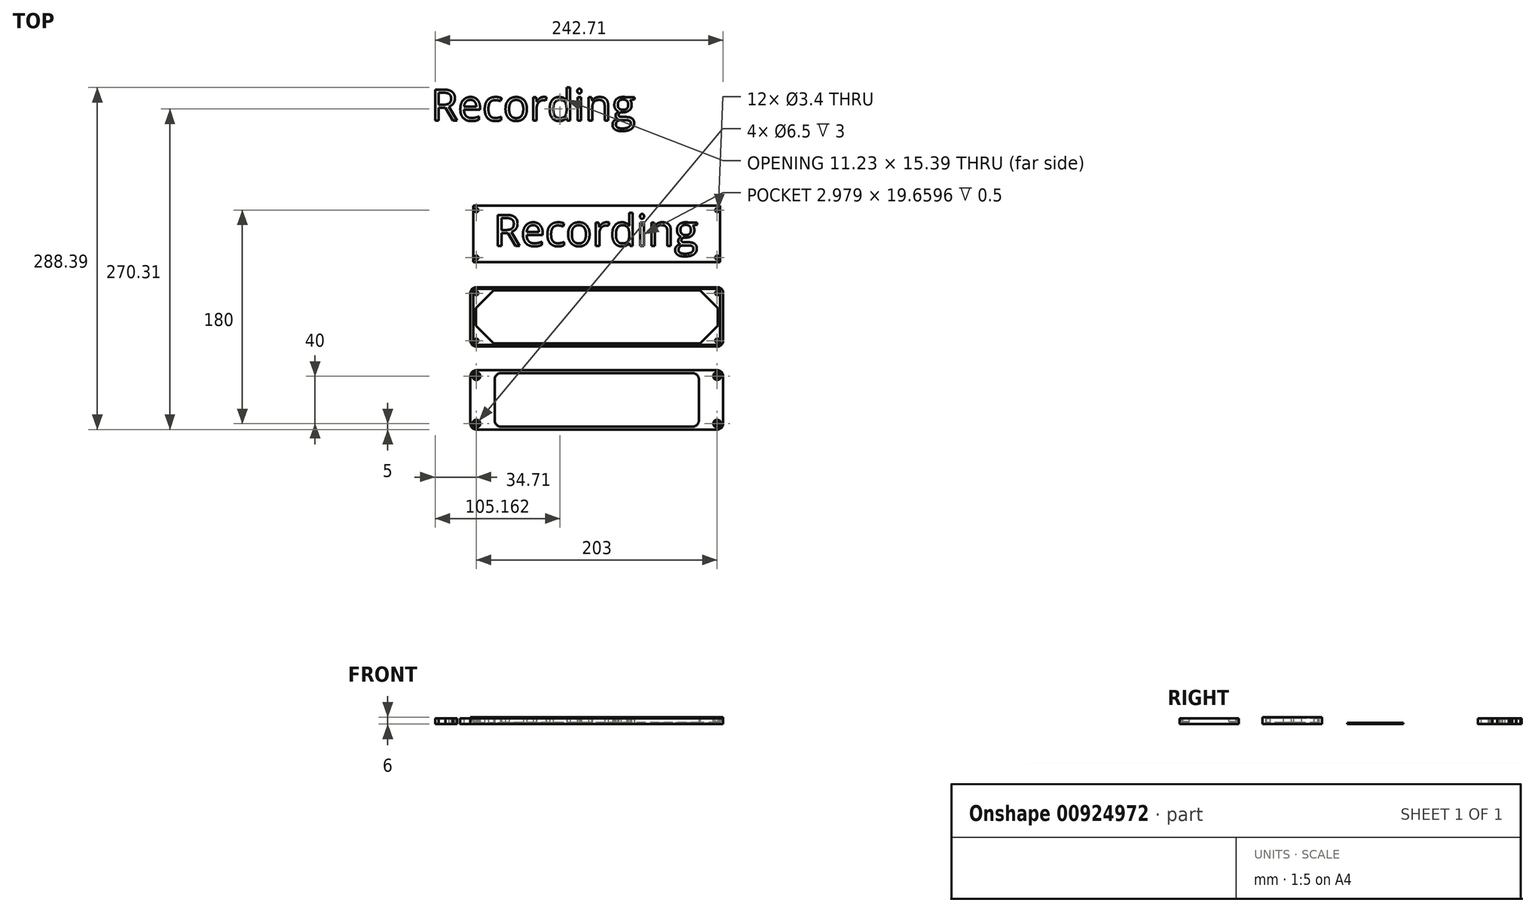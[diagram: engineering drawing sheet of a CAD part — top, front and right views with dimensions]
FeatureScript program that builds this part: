
annotation { "Feature Type Name" : "Feature", "Feature Type Description" : "" }
export const myFeature = defineFeature(function(context is Context, id is Id, definition is map)
    precondition{}
    {
        {
            var Q0;
            Q0=qCreatedBy(makeId("Top.planeOp"),FACE);
            var sketch = newSketch(context, id + "F0", { "sketchPlane" : qUnion([Q0])});
            skLineSegment(sketch, "E0.bottom", {"start": v(0, 0) * mm, "end": v(87, 0) * mm});
            skLineSegment(sketch, "E0.top", {"start": v(0, -45) * mm, "end": v(87, -45) * mm});
            skLineSegment(sketch, "E1.bottom", {"start": v(0, 0) * mm, "end": v(-87, 0) * mm});
            skLineSegment(sketch, "E1.top", {"start": v(0, -45) * mm, "end": v(-87, -45) * mm});
            skLineSegment(sketch, "E2", {"start": v(87, 0) * mm, "end": v(102, -15) * mm});
            skLineSegment(sketch, "E3", {"start": v(102, -15) * mm, "end": v(102, -30) * mm});
            skLineSegment(sketch, "E4", {"start": v(102, -30) * mm, "end": v(87, -45) * mm});
            skLineSegment(sketch, "E5", {"start": v(-87, 0) * mm, "end": v(-102, -15) * mm});
            skLineSegment(sketch, "E6", {"start": v(-102, -15) * mm, "end": v(-102, -30) * mm});
            skLineSegment(sketch, "E7", {"start": v(-102, -30) * mm, "end": v(-87, -45) * mm});
            skLineSegment(sketch, "E8.bottom", {"start": v(102, -21.5) * mm, "end": v(104, -21.5) * mm});
            skLineSegment(sketch, "E8.top", {"start": v(102, -23.5) * mm, "end": v(104, -23.5) * mm});
            skLineSegment(sketch, "E8.left", {"start": v(102, -21.5) * mm, "end": v(102, -23.5) * mm});
            skLineSegment(sketch, "E8.right", {"start": v(104, -21.5) * mm, "end": v(104, -23.5) * mm});
            skLineSegment(sketch, "E9.bottom", {"start": v(-102, -21.5) * mm, "end": v(-104, -21.5) * mm});
            skLineSegment(sketch, "E9.top", {"start": v(-102, -23.5) * mm, "end": v(-104, -23.5) * mm});
            skLineSegment(sketch, "E9.left", {"start": v(-102, -21.5) * mm, "end": v(-102, -23.5) * mm});
            skLineSegment(sketch, "E9.right", {"start": v(-104, -21.5) * mm, "end": v(-104, -23.5) * mm});
            skLineSegment(sketch, "E10.bottom", {"start": v(106.5, 2.5) * mm, "end": v(-106.5, 2.5) * mm});
            skLineSegment(sketch, "E10.top", {"start": v(106.5, -47.5) * mm, "end": v(-106.5, -47.5) * mm});
            skLineSegment(sketch, "E10.left", {"start": v(106.5, 2.5) * mm, "end": v(106.5, -47.5) * mm});
            skLineSegment(sketch, "E10.right", {"start": v(-106.5, 2.5) * mm, "end": v(-106.5, -47.5) * mm});
            skSolve(sketch);
        }
        {
            var Q0;
            Q0 = qSketchRegion(id + "F0", true);
            extrude(context, id + "F1", {"entities" : qUnion([Q0]), "depth" : 5 * mm, "offsetDistance" : 25 * mm});
        }
        {
            var Q0;
            Q0=makeQuery(id+"F0.imprint","IMPRINT",FACE,{"disambiguationData":[TD([[makeQuery(id+"F0.imprint","IMPRINT",EDGE,{"derivedFrom":sQuery(id+"F0.wireOp",EDGE,"E0.bottom")}),-1.0]])]});
            extrude(context, id + "F2", {"entities" : qUnion([Q0]), "operationType" : NewBodyOperationType.ADD, "depth" : 1.4 * mm, "offsetDistance" : 25 * mm});
        }
        {
            var Q0;
            Q0=makeQuery(id+"F1.opExtrude","CAP_FACE",FACE,{"disambiguationData":[OSD([sQuery(id+"F0.wireOp",EDGE,"E0.bottom"),sQuery(id+"F0.wireOp",EDGE,"E0.top"),sQuery(id+"F0.wireOp",EDGE,"E1.bottom"),sQuery(id+"F0.wireOp",EDGE,"E1.top"),sQuery(id+"F0.wireOp",EDGE,"E2"),sQuery(id+"F0.wireOp",EDGE,"E3"),sQuery(id+"F0.wireOp",EDGE,"E4"),sQuery(id+"F0.wireOp",EDGE,"E5"),sQuery(id+"F0.wireOp",EDGE,"E6"),sQuery(id+"F0.wireOp",EDGE,"E7"),sQuery(id+"F0.wireOp",EDGE,"E8.bottom"),sQuery(id+"F0.wireOp",EDGE,"E8.top"),sQuery(id+"F0.wireOp",EDGE,"E8.right"),sQuery(id+"F0.wireOp",EDGE,"E9.bottom"),sQuery(id+"F0.wireOp",EDGE,"E9.top"),sQuery(id+"F0.wireOp",EDGE,"E9.right"),sQuery(id+"F0.wireOp",EDGE,"E10.bottom"),sQuery(id+"F0.wireOp",EDGE,"E10.top"),sQuery(id+"F0.wireOp",EDGE,"E10.left"),sQuery(id+"F0.wireOp",EDGE,"E10.right")])],"isStart":false});
            var sketch = newSketch(context, id + "F3", { "sketchPlane" : qUnion([Q0])});
            skLineSegment(sketch, "E11.bottom", {"start": v(-106.5, 2.5) * mm, "end": v(106.5, 2.5) * mm});
            skLineSegment(sketch, "E11.top", {"start": v(-106.5, -47.5) * mm, "end": v(106.5, -47.5) * mm});
            skLineSegment(sketch, "E11.left", {"start": v(-106.5, 2.5) * mm, "end": v(-106.5, -47.5) * mm});
            skLineSegment(sketch, "E11.right", {"start": v(106.5, 2.5) * mm, "end": v(106.5, -47.5) * mm});
            skLineSegment(sketch, "E12.bottom", {"start": v(-104, 1.25) * mm, "end": v(104, 1.25) * mm});
            skLineSegment(sketch, "E12.top", {"start": v(-104, -46.25) * mm, "end": v(104, -46.25) * mm});
            skLineSegment(sketch, "E12.left", {"start": v(-104, 1.25) * mm, "end": v(-104, -46.25) * mm});
            skLineSegment(sketch, "E12.right", {"start": v(104, 1.25) * mm, "end": v(104, -46.25) * mm});
            skSolve(sketch);
        }
        {
            var Q0;
            Q0=makeQuery(id+"F3.imprint","IMPRINT",FACE,{"disambiguationData":[TD([[makeQuery(id+"F3.imprint","IMPRINT",EDGE,{"derivedFrom":sQuery(id+"F3.wireOp",EDGE,"E11.bottom")}),1.0]])]});
            extrude(context, id + "F4", {"entities" : qUnion([Q0]), "operationType" : NewBodyOperationType.ADD, "depth" : 1 * mm, "offsetDistance" : 25 * mm});
        }
        {
            var Q0;
            Q0=makeQuery(id+"F4.opExtrude","CAP_FACE",FACE,{"disambiguationData":[OSD([sQuery(id+"F3.wireOp",EDGE,"E11.bottom"),sQuery(id+"F3.wireOp",EDGE,"E11.top"),sQuery(id+"F3.wireOp",EDGE,"E11.left"),sQuery(id+"F3.wireOp",EDGE,"E11.right"),sQuery(id+"F3.wireOp",EDGE,"p96hWnhM-O248-CkP6-rmGI-8VL5oQeekFGz.bottom"),sQuery(id+"F3.wireOp",EDGE,"p96hWnhM-O248-CkP6-rmGI-8VL5oQeekFGz.top"),sQuery(id+"F3.wireOp",EDGE,"tadGcO1i-splK-dY1s-Agr0-QRfTQJM7h8ux"),sQuery(id+"F3.wireOp",EDGE,"MCb5JSWs-usyO-wEvL-fpDv-uoKTlJ5k66d6"),sQuery(id+"F3.wireOp",EDGE,"NITJUnnU-xe1N-w4uj-sHKg-5JDy11YuTqra"),sQuery(id+"F3.wireOp",EDGE,"5tmfxtAg-Ul8O-jr4B-bajV-lyweOX73wN6o"),sQuery(id+"F3.wireOp",EDGE,"gdZn3bBH-IIBM-45FK-eHiO-CvuzcM1Qr1wt"),sQuery(id+"F3.wireOp",EDGE,"ff11BVGO-ZWvE-YObo-sifm-qKeFPP4lbaiZ")])],"isStart":false});
            var sketch = newSketch(context, id + "F5", { "sketchPlane" : qUnion([Q0])});
            skLineSegment(sketch, "E13.bottom", {"start": v(-106.5, 2.5) * mm, "end": v(-96.5, 2.5) * mm, "construction": true});
            skLineSegment(sketch, "E13.top", {"start": v(-106.5, -7.5) * mm, "end": v(-96.5, -7.5) * mm, "construction": true});
            skLineSegment(sketch, "E13.left", {"start": v(-106.5, 2.5) * mm, "end": v(-106.5, -7.5) * mm, "construction": true});
            skLineSegment(sketch, "E13.right", {"start": v(-96.5, 2.5) * mm, "end": v(-96.5, -7.5) * mm, "construction": true});
            skLineSegment(sketch, "E14.bottom", {"start": v(-106.5, -47.5) * mm, "end": v(-96.5, -47.5) * mm, "construction": true});
            skLineSegment(sketch, "E14.top", {"start": v(-106.5, -37.5) * mm, "end": v(-96.5, -37.5) * mm, "construction": true});
            skLineSegment(sketch, "E14.left", {"start": v(-106.5, -47.5) * mm, "end": v(-106.5, -37.5) * mm, "construction": true});
            skLineSegment(sketch, "E14.right", {"start": v(-96.5, -47.5) * mm, "end": v(-96.5, -37.5) * mm, "construction": true});
            skLineSegment(sketch, "E15.bottom", {"start": v(106.5, -47.5) * mm, "end": v(96.5, -47.5) * mm, "construction": true});
            skLineSegment(sketch, "E15.top", {"start": v(106.5, -37.5) * mm, "end": v(96.5, -37.5) * mm, "construction": true});
            skLineSegment(sketch, "E15.left", {"start": v(106.5, -47.5) * mm, "end": v(106.5, -37.5) * mm, "construction": true});
            skLineSegment(sketch, "E15.right", {"start": v(96.5, -47.5) * mm, "end": v(96.5, -37.5) * mm, "construction": true});
            skLineSegment(sketch, "E16.bottom", {"start": v(106.5, 2.5) * mm, "end": v(96.5, 2.5) * mm, "construction": true});
            skLineSegment(sketch, "E16.top", {"start": v(106.5, -7.5) * mm, "end": v(96.5, -7.5) * mm, "construction": true});
            skLineSegment(sketch, "E16.left", {"start": v(106.5, 2.5) * mm, "end": v(106.5, -7.5) * mm, "construction": true});
            skLineSegment(sketch, "E16.right", {"start": v(96.5, 2.5) * mm, "end": v(96.5, -7.5) * mm, "construction": true});
            skLineSegment(sketch, "E17", {"start": v(-106.5, 2.5) * mm, "end": v(-96.5, -7.5) * mm, "construction": true});
            skLineSegment(sketch, "E18", {"start": v(-106.5, -7.5) * mm, "end": v(-96.5, 2.5) * mm, "construction": true});
            skLineSegment(sketch, "E19", {"start": v(-106.5, -37.5) * mm, "end": v(-96.5, -47.5) * mm, "construction": true});
            skLineSegment(sketch, "E20", {"start": v(-106.5, -47.5) * mm, "end": v(-96.5, -37.5) * mm, "construction": true});
            skLineSegment(sketch, "E21", {"start": v(96.5, -47.5) * mm, "end": v(106.5, -37.5) * mm, "construction": true});
            skLineSegment(sketch, "E22", {"start": v(96.5, -37.5) * mm, "end": v(106.5, -47.5) * mm, "construction": true});
            skLineSegment(sketch, "E23", {"start": v(96.5, 2.5) * mm, "end": v(106.5, -7.5) * mm, "construction": true});
            skLineSegment(sketch, "E24", {"start": v(96.5, -7.5) * mm, "end": v(106.5, 2.5) * mm, "construction": true});
            skPoint(sketch, "E25", {"position": v(-101.5, -2.5) * mm});
            skPoint(sketch, "E26", {"position": v(-101.5, -42.5) * mm});
            skPoint(sketch, "E27", {"position": v(101.5, -2.5) * mm});
            skPoint(sketch, "E28", {"position": v(101.5, -42.5) * mm});
            skSolve(sketch);
        }
        {
            var Q0;
            Q0=sQuery(id+"F5.wireOp",VERTEX,"E25");
            var Q1;
            Q1=sQuery(id+"F5.wireOp",VERTEX,"E26");
            var Q2;
            Q2=sQuery(id+"F5.wireOp",VERTEX,"E28");
            var Q3;
            Q3=sQuery(id+"F5.wireOp",VERTEX,"E27");
            var Q4;
            Q4=makeQuery(id+"F1.opExtrude","SWEPT_BODY",BODY,{"disambiguationData":[OSD([sQuery(id+"F0.wireOp",EDGE,"E0.bottom"),sQuery(id+"F0.wireOp",EDGE,"E0.top"),sQuery(id+"F0.wireOp",EDGE,"E1.bottom"),sQuery(id+"F0.wireOp",EDGE,"E1.top"),sQuery(id+"F0.wireOp",EDGE,"E2"),sQuery(id+"F0.wireOp",EDGE,"E3"),sQuery(id+"F0.wireOp",EDGE,"E4"),sQuery(id+"F0.wireOp",EDGE,"E5"),sQuery(id+"F0.wireOp",EDGE,"E6"),sQuery(id+"F0.wireOp",EDGE,"E7"),sQuery(id+"F0.wireOp",EDGE,"E8.bottom"),sQuery(id+"F0.wireOp",EDGE,"E8.top"),sQuery(id+"F0.wireOp",EDGE,"E8.right"),sQuery(id+"F0.wireOp",EDGE,"E9.bottom"),sQuery(id+"F0.wireOp",EDGE,"E9.top"),sQuery(id+"F0.wireOp",EDGE,"E9.right"),sQuery(id+"F0.wireOp",EDGE,"E10.bottom"),sQuery(id+"F0.wireOp",EDGE,"E10.top"),sQuery(id+"F0.wireOp",EDGE,"E10.left"),sQuery(id+"F0.wireOp",EDGE,"E10.right")])]});
            hole(context, id + "F6", {"style" : HoleStyle.SIMPLE, "endStyle" : HoleEndStyle.BLIND, "standardTappedOrClearance" : lookupTablePath({ "fit" : "Normal", "standard" : "ISO", "size" : "M3", "type" : "Clearance" }), "standardBlindInLast" : lookupTablePath({ "fit" : "Normal", "standard" : "ISO", "engagement" : "75%", "pitch" : "0.5 mm", "size" : "M3", "type" : "Clearance & tapped" }), "holeDiameter" : 3.4 * mm, "majorDiameter" : 5 * mm, "holeDepth" : 7 * mm, "isTappedThrough" : true, "tappedDepth" : 12 * mm, "tapClearance" : 3, "startFromSketch" : true, "locations" : qUnion([Q0, Q1, Q2, Q3]), "scope" : qUnion([Q4])});
        }
        {
            var Q0;
            Q0=makeQuery(id+"F1.opExtrude","SWEPT_EDGE",EDGE,{"disambiguationData":[OSD([sQuery(id+"F0.wireOp",EDGE,"E10.bottom"),sQuery(id+"F0.wireOp",EDGE,"E10.right")])]});
            var Q1;
            Q1=makeQuery(id+"F1.opExtrude","SWEPT_EDGE",EDGE,{"disambiguationData":[OSD([sQuery(id+"F0.wireOp",EDGE,"E10.top"),sQuery(id+"F0.wireOp",EDGE,"E10.right")])]});
            var Q2;
            Q2=makeQuery(id+"F1.opExtrude","SWEPT_EDGE",EDGE,{"disambiguationData":[OSD([sQuery(id+"F0.wireOp",EDGE,"E10.top"),sQuery(id+"F0.wireOp",EDGE,"E10.left")])]});
            var Q3;
            Q3=makeQuery(id+"F1.opExtrude","SWEPT_EDGE",EDGE,{"disambiguationData":[OSD([sQuery(id+"F0.wireOp",EDGE,"E10.bottom"),sQuery(id+"F0.wireOp",EDGE,"E10.left")])]});
            fillet(context, id + "F7", {"entities" : qUnion([Q0, Q1, Q2, Q3]), "radius" : 5 * mm, "tangentPropagation" : true, "allowEdgeOverflow" : false});
        }
        {
            var Q0;
            Q0=qCreatedBy(makeId("Top.planeOp"),FACE);
            var sketch = newSketch(context, id + "F8", { "sketchPlane" : qUnion([Q0])});
            skLineSegment(sketch, "E29.bottom", {"start": v(-86, -70) * mm, "end": v(86, -70) * mm});
            skLineSegment(sketch, "E29.top", {"start": v(-86, -115) * mm, "end": v(86, -115) * mm});
            skLineSegment(sketch, "E29.left", {"start": v(-86, -70) * mm, "end": v(-86, -115) * mm});
            skLineSegment(sketch, "E29.right", {"start": v(86, -70) * mm, "end": v(86, -115) * mm});
            skLineSegment(sketch, "E30.bottom", {"start": v(-106.5, -67.5) * mm, "end": v(106.5, -67.5) * mm});
            skLineSegment(sketch, "E30.top", {"start": v(-106.5, -117.5) * mm, "end": v(106.5, -117.5) * mm});
            skLineSegment(sketch, "E30.left", {"start": v(-106.5, -67.5) * mm, "end": v(-106.5, -117.5) * mm});
            skLineSegment(sketch, "E30.right", {"start": v(106.5, -67.5) * mm, "end": v(106.5, -117.5) * mm});
            skSolve(sketch);
        }
        {
            var Q0;
            Q0=makeQuery(id+"F8.imprint","IMPRINT",FACE,{"disambiguationData":[TD([[makeQuery(id+"F8.imprint","IMPRINT",EDGE,{"derivedFrom":sQuery(id+"F8.wireOp",EDGE,"E29.bottom")}),1.0]])]});
            extrude(context, id + "F9", {"entities" : qUnion([Q0]), "depth" : 5 * mm, "offsetDistance" : 25 * mm});
        }
        {
            var Q0;
            Q0=makeQuery(id+"F9.opExtrude","CAP_FACE",FACE,{"disambiguationData":[OSD([sQuery(id+"F8.wireOp",EDGE,"E29.bottom"),sQuery(id+"F8.wireOp",EDGE,"E29.top"),sQuery(id+"F8.wireOp",EDGE,"E29.left"),sQuery(id+"F8.wireOp",EDGE,"E29.right"),sQuery(id+"F8.wireOp",EDGE,"E30.bottom"),sQuery(id+"F8.wireOp",EDGE,"E30.top"),sQuery(id+"F8.wireOp",EDGE,"E30.left"),sQuery(id+"F8.wireOp",EDGE,"E30.right")])],"isStart":false});
            var sketch = newSketch(context, id + "F10", { "sketchPlane" : qUnion([Q0])});
            skLineSegment(sketch, "E31.bottom", {"start": v(-106.5, -67.5) * mm, "end": v(-96.5, -67.5) * mm, "construction": true});
            skLineSegment(sketch, "E31.top", {"start": v(-106.5, -77.5) * mm, "end": v(-96.5, -77.5) * mm, "construction": true});
            skLineSegment(sketch, "E31.left", {"start": v(-106.5, -67.5) * mm, "end": v(-106.5, -77.5) * mm, "construction": true});
            skLineSegment(sketch, "E31.right", {"start": v(-96.5, -67.5) * mm, "end": v(-96.5, -77.5) * mm, "construction": true});
            skLineSegment(sketch, "E32.bottom", {"start": v(-106.5, -117.5) * mm, "end": v(-96.5, -117.5) * mm, "construction": true});
            skLineSegment(sketch, "E32.top", {"start": v(-106.5, -107.5) * mm, "end": v(-96.5, -107.5) * mm, "construction": true});
            skLineSegment(sketch, "E32.left", {"start": v(-106.5, -117.5) * mm, "end": v(-106.5, -107.5) * mm, "construction": true});
            skLineSegment(sketch, "E32.right", {"start": v(-96.5, -117.5) * mm, "end": v(-96.5, -107.5) * mm, "construction": true});
            skLineSegment(sketch, "E33.bottom", {"start": v(106.5, -117.5) * mm, "end": v(96.5, -117.5) * mm, "construction": true});
            skLineSegment(sketch, "E33.top", {"start": v(106.5, -107.5) * mm, "end": v(96.5, -107.5) * mm, "construction": true});
            skLineSegment(sketch, "E33.left", {"start": v(106.5, -117.5) * mm, "end": v(106.5, -107.5) * mm, "construction": true});
            skLineSegment(sketch, "E33.right", {"start": v(96.5, -117.5) * mm, "end": v(96.5, -107.5) * mm, "construction": true});
            skLineSegment(sketch, "E34.bottom", {"start": v(106.5, -67.5) * mm, "end": v(96.5, -67.5) * mm, "construction": true});
            skLineSegment(sketch, "E34.top", {"start": v(106.5, -77.5) * mm, "end": v(96.5, -77.5) * mm, "construction": true});
            skLineSegment(sketch, "E34.left", {"start": v(106.5, -67.5) * mm, "end": v(106.5, -77.5) * mm, "construction": true});
            skLineSegment(sketch, "E34.right", {"start": v(96.5, -67.5) * mm, "end": v(96.5, -77.5) * mm, "construction": true});
            skLineSegment(sketch, "E35", {"start": v(-106.5, -67.5) * mm, "end": v(-96.5, -77.5) * mm, "construction": true});
            skLineSegment(sketch, "E36", {"start": v(-106.5, -77.5) * mm, "end": v(-96.5, -67.5) * mm, "construction": true});
            skLineSegment(sketch, "E37", {"start": v(-106.5, -107.5) * mm, "end": v(-96.5, -117.5) * mm, "construction": true});
            skLineSegment(sketch, "E38", {"start": v(-106.5, -117.5) * mm, "end": v(-96.5, -107.5) * mm, "construction": true});
            skLineSegment(sketch, "E39", {"start": v(96.5, -107.5) * mm, "end": v(106.5, -117.5) * mm, "construction": true});
            skLineSegment(sketch, "E40", {"start": v(96.5, -117.5) * mm, "end": v(106.5, -107.5) * mm, "construction": true});
            skLineSegment(sketch, "E41", {"start": v(106.5, -67.5) * mm, "end": v(96.5, -77.5) * mm, "construction": true});
            skLineSegment(sketch, "E42", {"start": v(96.5, -67.5) * mm, "end": v(106.5, -77.5) * mm, "construction": true});
            skPoint(sketch, "E43", {"position": v(-101.5, -72.5) * mm});
            skPoint(sketch, "E44", {"position": v(-101.5, -112.5) * mm});
            skPoint(sketch, "E45", {"position": v(101.5, -72.5) * mm});
            skPoint(sketch, "E46", {"position": v(101.5, -112.5) * mm});
            skSolve(sketch);
        }
        {
            var Q0;
            Q0=sQuery(id+"F10.wireOp",VERTEX,"E43");
            var Q1;
            Q1=sQuery(id+"F10.wireOp",VERTEX,"E44");
            var Q2;
            Q2=sQuery(id+"F10.wireOp",VERTEX,"E45");
            var Q3;
            Q3=sQuery(id+"F10.wireOp",VERTEX,"E46");
            var Q4;
            Q4=makeQuery(id+"F9.opExtrude","SWEPT_BODY",BODY,{"disambiguationData":[OSD([sQuery(id+"F8.wireOp",EDGE,"E29.bottom"),sQuery(id+"F8.wireOp",EDGE,"E29.top"),sQuery(id+"F8.wireOp",EDGE,"E29.left"),sQuery(id+"F8.wireOp",EDGE,"E29.right"),sQuery(id+"F8.wireOp",EDGE,"E30.bottom"),sQuery(id+"F8.wireOp",EDGE,"E30.top"),sQuery(id+"F8.wireOp",EDGE,"E30.left"),sQuery(id+"F8.wireOp",EDGE,"E30.right")])]});
            hole(context, id + "F11", {"style" : HoleStyle.C_BORE, "endStyle" : HoleEndStyle.BLIND, "standardTappedOrClearance" : lookupTablePath({ "fit" : "Normal", "standard" : "ISO", "size" : "M3", "type" : "Clearance" }), "standardBlindInLast" : lookupTablePath({ "fit" : "Normal", "standard" : "ISO", "engagement" : "75%", "pitch" : "0.5 mm", "size" : "M3", "type" : "Clearance & tapped" }), "holeDiameter" : 3.4 * mm, "cBoreDiameter" : 6.5 * mm, "cBoreDepth" : 3 * mm, "majorDiameter" : 5 * mm, "holeDepth" : 5 * mm, "isTappedThrough" : true, "tappedDepth" : 12 * mm, "tapClearance" : 3, "startFromSketch" : true, "locations" : qUnion([Q0, Q1, Q2, Q3]), "scope" : qUnion([Q4])});
        }
        {
            var Q0;
            Q0=makeQuery(id+"F9.opExtrude","SWEPT_EDGE",EDGE,{"disambiguationData":[OSD([sQuery(id+"F8.wireOp",EDGE,"E29.bottom"),sQuery(id+"F8.wireOp",EDGE,"E29.left")])]});
            var Q1;
            Q1=makeQuery(id+"F9.opExtrude","SWEPT_EDGE",EDGE,{"disambiguationData":[OSD([sQuery(id+"F8.wireOp",EDGE,"E29.top"),sQuery(id+"F8.wireOp",EDGE,"E29.left")])]});
            var Q2;
            Q2=makeQuery(id+"F9.opExtrude","SWEPT_EDGE",EDGE,{"disambiguationData":[OSD([sQuery(id+"F8.wireOp",EDGE,"E29.bottom"),sQuery(id+"F8.wireOp",EDGE,"E29.right")])]});
            var Q3;
            Q3=makeQuery(id+"F9.opExtrude","SWEPT_EDGE",EDGE,{"disambiguationData":[OSD([sQuery(id+"F8.wireOp",EDGE,"E29.top"),sQuery(id+"F8.wireOp",EDGE,"E29.right")])]});
            var Q4;
            Q4=makeQuery(id+"F9.opExtrude","SWEPT_EDGE",EDGE,{"disambiguationData":[OSD([sQuery(id+"F8.wireOp",EDGE,"E30.top"),sQuery(id+"F8.wireOp",EDGE,"E30.right")])]});
            var Q5;
            Q5=makeQuery(id+"F9.opExtrude","SWEPT_EDGE",EDGE,{"disambiguationData":[OSD([sQuery(id+"F8.wireOp",EDGE,"E30.bottom"),sQuery(id+"F8.wireOp",EDGE,"E30.right")])]});
            var Q6;
            Q6=makeQuery(id+"F9.opExtrude","SWEPT_EDGE",EDGE,{"disambiguationData":[OSD([sQuery(id+"F8.wireOp",EDGE,"E30.top"),sQuery(id+"F8.wireOp",EDGE,"E30.left")])]});
            var Q7;
            Q7=makeQuery(id+"F9.opExtrude","SWEPT_EDGE",EDGE,{"disambiguationData":[OSD([sQuery(id+"F8.wireOp",EDGE,"E30.bottom"),sQuery(id+"F8.wireOp",EDGE,"E30.left")])]});
            fillet(context, id + "F12", {"entities" : qUnion([Q0, Q1, Q2, Q3, Q4, Q5, Q6, Q7]), "radius" : 5 * mm, "tangentPropagation" : true, "allowEdgeOverflow" : false});
        }
        {
            var Q0;
            Q0=makeQuery(id+"F9.opExtrude","CAP_EDGE",EDGE,{"disambiguationData":[OSD([sQuery(id+"F8.wireOp",EDGE,"E29.bottom")])],"isStart":false});
            var Q1;
            Q1=makeQuery(id+"F9.opExtrude","CAP_EDGE",EDGE,{"disambiguationData":[OSD([sQuery(id+"F8.wireOp",EDGE,"E30.bottom")])],"isStart":false});
            fillet(context, id + "F13", {"entities" : qUnion([Q0, Q1]), "radius" : 1 * mm, "tangentPropagation" : true, "allowEdgeOverflow" : false});
        }
        {
            var Q0;
            Q0=qCreatedBy(makeId("Top.planeOp"),FACE);
            var sketch = newSketch(context, id + "F14", { "sketchPlane" : qUnion([Q0])});
            skLineSegment(sketch, "E47.bottom", {"start": v(-106.5, 72.5) * mm, "end": v(106.5, 72.5) * mm, "construction": true});
            skLineSegment(sketch, "E47.top", {"start": v(-106.5, 22.5) * mm, "end": v(106.5, 22.5) * mm, "construction": true});
            skLineSegment(sketch, "E47.left", {"start": v(-106.5, 72.5) * mm, "end": v(-106.5, 22.5) * mm, "construction": true});
            skLineSegment(sketch, "E47.right", {"start": v(106.5, 72.5) * mm, "end": v(106.5, 22.5) * mm, "construction": true});
            skLineSegment(sketch, "E48.bottom", {"start": v(-104, 71.25) * mm, "end": v(104, 71.25) * mm});
            skLineSegment(sketch, "E48.top", {"start": v(-104, 23.75) * mm, "end": v(104, 23.75) * mm});
            skLineSegment(sketch, "E48.left", {"start": v(-104, 71.25) * mm, "end": v(-104, 23.75) * mm});
            skLineSegment(sketch, "E48.right", {"start": v(104, 71.25) * mm, "end": v(104, 23.75) * mm});
            skSolve(sketch);
        }
        {
            var Q0;
            Q0 = qSketchRegion(id + "F14", true);
            extrude(context, id + "F15", {"entities" : qUnion([Q0]), "depth" : 1 * mm, "offsetDistance" : 25 * mm});
        }
        {
            var Q0;
            Q0=makeQuery(id+"F15.opExtrude","CAP_FACE",FACE,{"disambiguationData":[OSD([sQuery(id+"F14.wireOp",EDGE,"E48.bottom"),sQuery(id+"F14.wireOp",EDGE,"E48.top"),sQuery(id+"F14.wireOp",EDGE,"E48.left"),sQuery(id+"F14.wireOp",EDGE,"E48.right")])],"isStart":false});
            var sketch = newSketch(context, id + "F16", { "sketchPlane" : qUnion([Q0])});
            skLineSegment(sketch, "E49.bottom", {"start": v(-106.5, 72.5) * mm, "end": v(106.5, 72.5) * mm, "construction": true});
            skLineSegment(sketch, "E49.top", {"start": v(-106.5, 22.5) * mm, "end": v(106.5, 22.5) * mm, "construction": true});
            skLineSegment(sketch, "E49.left", {"start": v(-106.5, 72.5) * mm, "end": v(-106.5, 22.5) * mm, "construction": true});
            skLineSegment(sketch, "E49.right", {"start": v(106.5, 72.5) * mm, "end": v(106.5, 22.5) * mm, "construction": true});
            skLineSegment(sketch, "E50.bottom", {"start": v(106.5, 22.5) * mm, "end": v(96.5, 22.5) * mm, "construction": true});
            skLineSegment(sketch, "E50.top", {"start": v(106.5, 32.5) * mm, "end": v(96.5, 32.5) * mm, "construction": true});
            skLineSegment(sketch, "E50.left", {"start": v(106.5, 22.5) * mm, "end": v(106.5, 32.5) * mm, "construction": true});
            skLineSegment(sketch, "E50.right", {"start": v(96.5, 22.5) * mm, "end": v(96.5, 32.5) * mm, "construction": true});
            skLineSegment(sketch, "E51.bottom", {"start": v(106.5, 72.5) * mm, "end": v(96.5, 72.5) * mm, "construction": true});
            skLineSegment(sketch, "E51.top", {"start": v(106.5, 62.5) * mm, "end": v(96.5, 62.5) * mm, "construction": true});
            skLineSegment(sketch, "E51.left", {"start": v(106.5, 72.5) * mm, "end": v(106.5, 62.5) * mm, "construction": true});
            skLineSegment(sketch, "E51.right", {"start": v(96.5, 72.5) * mm, "end": v(96.5, 62.5) * mm, "construction": true});
            skLineSegment(sketch, "E52.bottom", {"start": v(-106.5, 72.5) * mm, "end": v(-96.5, 72.5) * mm, "construction": true});
            skLineSegment(sketch, "E52.top", {"start": v(-106.5, 62.5) * mm, "end": v(-96.5, 62.5) * mm, "construction": true});
            skLineSegment(sketch, "E52.left", {"start": v(-106.5, 72.5) * mm, "end": v(-106.5, 62.5) * mm, "construction": true});
            skLineSegment(sketch, "E52.right", {"start": v(-96.5, 72.5) * mm, "end": v(-96.5, 62.5) * mm, "construction": true});
            skLineSegment(sketch, "E53.bottom", {"start": v(-106.5, 22.5) * mm, "end": v(-96.5, 22.5) * mm, "construction": true});
            skLineSegment(sketch, "E53.top", {"start": v(-106.5, 32.5) * mm, "end": v(-96.5, 32.5) * mm, "construction": true});
            skLineSegment(sketch, "E53.left", {"start": v(-106.5, 22.5) * mm, "end": v(-106.5, 32.5) * mm, "construction": true});
            skLineSegment(sketch, "E53.right", {"start": v(-96.5, 22.5) * mm, "end": v(-96.5, 32.5) * mm, "construction": true});
            skLineSegment(sketch, "E54", {"start": v(-106.5, 72.5) * mm, "end": v(-96.5, 62.5) * mm, "construction": true});
            skLineSegment(sketch, "E55", {"start": v(-106.5, 62.5) * mm, "end": v(-96.5, 72.5) * mm, "construction": true});
            skLineSegment(sketch, "E56", {"start": v(-106.5, 32.5) * mm, "end": v(-96.5, 22.5) * mm, "construction": true});
            skLineSegment(sketch, "E57", {"start": v(-106.5, 22.5) * mm, "end": v(-96.5, 32.5) * mm, "construction": true});
            skLineSegment(sketch, "E58", {"start": v(96.5, 32.5) * mm, "end": v(106.5, 22.5) * mm, "construction": true});
            skLineSegment(sketch, "E59", {"start": v(96.5, 22.5) * mm, "end": v(106.5, 32.5) * mm, "construction": true});
            skLineSegment(sketch, "E60", {"start": v(96.5, 62.5) * mm, "end": v(106.5, 72.5) * mm, "construction": true});
            skLineSegment(sketch, "E61", {"start": v(96.5, 72.5) * mm, "end": v(106.5, 62.5) * mm, "construction": true});
            skPoint(sketch, "E62", {"position": v(-101.5, 67.5) * mm});
            skPoint(sketch, "E63", {"position": v(-101.5, 27.5) * mm});
            skPoint(sketch, "E64", {"position": v(101.5, 67.5) * mm});
            skPoint(sketch, "E65", {"position": v(101.5, 27.5) * mm});
            skSolve(sketch);
        }
        {
            var Q0;
            Q0=sQuery(id+"F16.wireOp",VERTEX,"E62");
            var Q1;
            Q1=sQuery(id+"F16.wireOp",VERTEX,"E63");
            var Q2;
            Q2=sQuery(id+"F16.wireOp",VERTEX,"E65");
            var Q3;
            Q3=sQuery(id+"F16.wireOp",VERTEX,"E64");
            var Q4;
            Q4=makeQuery(id+"F15.opExtrude","SWEPT_BODY",BODY,{"disambiguationData":[OSD([sQuery(id+"F14.wireOp",EDGE,"E48.bottom"),sQuery(id+"F14.wireOp",EDGE,"E48.top"),sQuery(id+"F14.wireOp",EDGE,"E48.left"),sQuery(id+"F14.wireOp",EDGE,"E48.right")])]});
            hole(context, id + "F17", {"style" : HoleStyle.SIMPLE, "endStyle" : HoleEndStyle.BLIND, "standardTappedOrClearance" : lookupTablePath({ "fit" : "Normal", "standard" : "ISO", "size" : "M3", "type" : "Clearance" }), "standardBlindInLast" : lookupTablePath({ "fit" : "Normal", "standard" : "ISO", "engagement" : "75%", "pitch" : "0.5 mm", "size" : "M3", "type" : "Clearance & tapped" }), "holeDiameter" : 3.4 * mm, "majorDiameter" : 5 * mm, "holeDepth" : 1 * mm, "isTappedThrough" : true, "tappedDepth" : 12 * mm, "tapClearance" : 3, "startFromSketch" : true, "locations" : qUnion([Q0, Q1, Q2, Q3]), "scope" : qUnion([Q4])});
        }
        {
            var Q0;
            Q0=makeQuery(id+"F15.opExtrude","CAP_FACE",FACE,{"disambiguationData":[OSD([sQuery(id+"F14.wireOp",EDGE,"E48.bottom"),sQuery(id+"F14.wireOp",EDGE,"E48.top"),sQuery(id+"F14.wireOp",EDGE,"E48.left"),sQuery(id+"F14.wireOp",EDGE,"E48.right")])],"isStart":false});
            var sketch = newSketch(context, id + "F18", { "sketchPlane" : qUnion([Q0])});
            skText(sketch, "E66", { "text": "Recording", "fontName": "OpenSans-Regular.ttf"});
            const initialGuessF18  = {"E66": [-0.087, 0.0373, 1, 0, 0.02645]};
            skSetInitialGuess(sketch, initialGuessF18);
            skSolve(sketch);
        }
        {
            var Q0;
            Q0 = qSketchRegion(id + "F18", true);
            extrude(context, id + "F19", {"entities" : qUnion([Q0]), "operationType" : NewBodyOperationType.REMOVE, "oppositeDirection" : true, "depth" : 0.5 * mm, "offsetDistance" : 25 * mm});
        }
        {
            var Q0;
            Q0=qCreatedBy(makeId("Top.planeOp"),FACE);
            var sketch = newSketch(context, id + "F20", { "sketchPlane" : qUnion([Q0])});
            skText(sketch, "E67", { "text": "Recording", "fontName": "OpenSans-Regular.ttf"});
            const initialGuessF20  = {"E67": [-0.13981, 0.14298, 1, 0, 0.02645]};
            skSetInitialGuess(sketch, initialGuessF20);
            skSolve(sketch);
        }
        {
            var Q0;
            Q0 = qSketchRegion(id + "F20", true);
            extrude(context, id + "F21", {"entities" : qUnion([Q0]), "depth" : 5 * mm, "offsetDistance" : 25 * mm});
        }
    });
